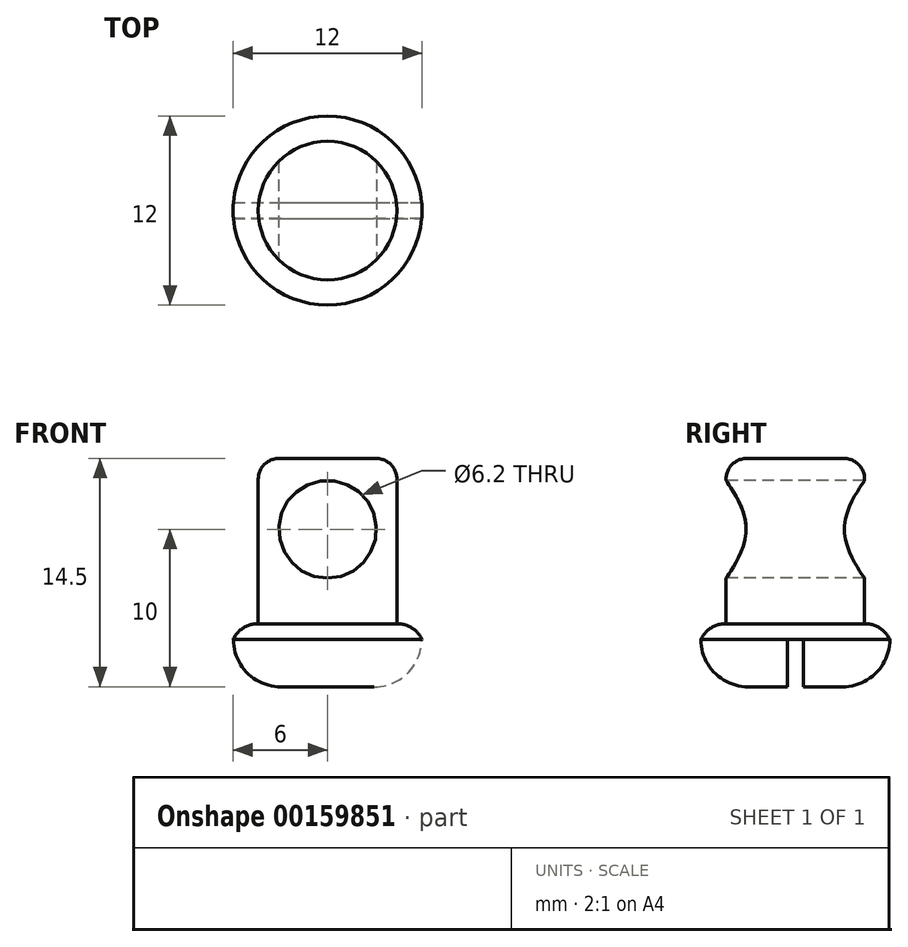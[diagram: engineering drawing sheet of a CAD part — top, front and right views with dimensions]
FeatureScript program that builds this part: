
annotation { "Feature Type Name" : "Feature", "Feature Type Description" : "" }
export const myFeature = defineFeature(function(context is Context, id is Id, definition is map)
    precondition{}
    {
        {
            var Q0;
            Q0=qCreatedBy(makeId("Top.planeOp"),FACE);
            var sketch = newSketch(context, id + "F0", { "sketchPlane" : qUnion([Q0])});
            skCircle(sketch, "E0", {"center": v(0, 0) * mm, "radius": 4.4 * mm});
            skCircle(sketch, "E1", {"center": v(0, 0) * mm, "radius": 6 * mm});
            skLineSegment(sketch, "E2", {"start": v(-5.98, 0.5) * mm, "end": v(5.98, 0.5) * mm});
            skLineSegment(sketch, "E3.MirrorCS", {"start": v(-5.98, -0.5) * mm, "end": v(5.98, -0.5) * mm});
            skSolve(sketch);
        }
        {
            var Q0;
            {var subQ0=sQuery(id+"F0.wireOp",EDGE,"E2");var subQ1=sQuery(id+"F0.wireOp",EDGE,"E0");var subQ2=makeQuery(id+"F0.imprint","INTERSECT",VERTEX,{"disambiguationData":[OD(0.0)],"derivedFrom":[subQ1,subQ0]});Q0=makeQuery(id+"F0.imprint","IMPRINT",FACE,{"disambiguationData":[TD([[makeQuery(id+"F0.imprint","IMPRINT",EDGE,{"disambiguationData":[TD([[subQ2,-1.0]])],"derivedFrom":subQ1}),1.0]])]});}
            var Q1;
            {var subQ0=sQuery(id+"F0.wireOp",EDGE,"E2");var subQ1=sQuery(id+"F0.wireOp",EDGE,"E0");var subQ2=makeQuery(id+"F0.imprint","INTERSECT",VERTEX,{"disambiguationData":[OD(0.0)],"derivedFrom":[subQ1,subQ0]});Q1=makeQuery(id+"F0.imprint","IMPRINT",FACE,{"disambiguationData":[TD([[makeQuery(id+"F0.imprint","IMPRINT",EDGE,{"disambiguationData":[TD([[subQ2,1.0]])],"derivedFrom":subQ1}),1.0]])]});}
            var Q2;
            {var subQ0=sQuery(id+"F0.wireOp",EDGE,"E3.MirrorCS");var subQ1=sQuery(id+"F0.wireOp",EDGE,"E0");var subQ2=makeQuery(id+"F0.imprint","INTERSECT",VERTEX,{"disambiguationData":[OD(0.0)],"derivedFrom":[subQ1,subQ0]});Q2=makeQuery(id+"F0.imprint","IMPRINT",FACE,{"disambiguationData":[TD([[makeQuery(id+"F0.imprint","IMPRINT",EDGE,{"disambiguationData":[TD([[subQ2,-1.0]])],"derivedFrom":subQ1}),1.0]])]});}
            extrude(context, id + "F1", {"entities" : qUnion([Q0, Q1, Q2]), "depth" : 14.5 * mm});
        }
        {
            var Q0;
            {var subQ0=sQuery(id+"F0.wireOp",EDGE,"E2");var subQ1=sQuery(id+"F0.wireOp",EDGE,"E0");var subQ2=makeQuery(id+"F0.imprint","INTERSECT",VERTEX,{"disambiguationData":[OD(0.0)],"derivedFrom":[subQ1,subQ0]});Q0=makeQuery(id+"F0.imprint","IMPRINT",FACE,{"disambiguationData":[TD([[makeQuery(id+"F0.imprint","IMPRINT",EDGE,{"disambiguationData":[TD([[subQ2,-1.0]])],"derivedFrom":subQ1}),-1.0]])]});}
            var Q1;
            {var subQ0=sQuery(id+"F0.wireOp",EDGE,"E3.MirrorCS");var subQ1=sQuery(id+"F0.wireOp",EDGE,"E0");var subQ2=makeQuery(id+"F0.imprint","INTERSECT",VERTEX,{"disambiguationData":[OD(0.0)],"derivedFrom":[subQ1,subQ0]});Q1=makeQuery(id+"F0.imprint","IMPRINT",FACE,{"disambiguationData":[TD([[makeQuery(id+"F0.imprint","IMPRINT",EDGE,{"disambiguationData":[TD([[subQ2,-1.0]])],"derivedFrom":subQ1}),-1.0]])]});}
            var Q2;
            {var subQ0=sQuery(id+"F0.wireOp",EDGE,"E2");var subQ1=sQuery(id+"F0.wireOp",EDGE,"E0");var subQ2=makeQuery(id+"F0.imprint","INTERSECT",VERTEX,{"disambiguationData":[OD(1.0)],"derivedFrom":[subQ1,subQ0]});Q2=makeQuery(id+"F0.imprint","IMPRINT",FACE,{"disambiguationData":[TD([[makeQuery(id+"F0.imprint","IMPRINT",EDGE,{"disambiguationData":[TD([[subQ2,1.0]])],"derivedFrom":subQ1}),-1.0]])]});}
            var Q3;
            {var subQ0=sQuery(id+"F0.wireOp",EDGE,"E2");var subQ1=sQuery(id+"F0.wireOp",EDGE,"E0");var subQ2=makeQuery(id+"F0.imprint","INTERSECT",VERTEX,{"disambiguationData":[OD(0.0)],"derivedFrom":[subQ1,subQ0]});Q3=makeQuery(id+"F0.imprint","IMPRINT",FACE,{"disambiguationData":[TD([[makeQuery(id+"F0.imprint","IMPRINT",EDGE,{"disambiguationData":[TD([[subQ2,1.0]])],"derivedFrom":subQ1}),-1.0]])]});}
            extrude(context, id + "F2", {"entities" : qUnion([Q0, Q1, Q2, Q3]), "operationType" : NewBodyOperationType.ADD, "depth" : 4 * mm});
        }
        {
            var Q0;
            {var subQ0=sQuery(id+"F0.wireOp",EDGE,"E2");var subQ1=sQuery(id+"F0.wireOp",EDGE,"E0");var subQ2=makeQuery(id+"F0.imprint","INTERSECT",VERTEX,{"disambiguationData":[OD(0.0)],"derivedFrom":[subQ1,subQ0]});Q0=makeQuery(id+"F0.imprint","IMPRINT",FACE,{"disambiguationData":[TD([[makeQuery(id+"F0.imprint","IMPRINT",EDGE,{"disambiguationData":[TD([[subQ2,-1.0]])],"derivedFrom":subQ1}),-1.0]])]});}
            var Q1;
            {var subQ0=sQuery(id+"F0.wireOp",EDGE,"E2");var subQ1=sQuery(id+"F0.wireOp",EDGE,"E0");var subQ2=makeQuery(id+"F0.imprint","INTERSECT",VERTEX,{"disambiguationData":[OD(0.0)],"derivedFrom":[subQ1,subQ0]});Q1=makeQuery(id+"F0.imprint","IMPRINT",FACE,{"disambiguationData":[TD([[makeQuery(id+"F0.imprint","IMPRINT",EDGE,{"disambiguationData":[TD([[subQ2,-1.0]])],"derivedFrom":subQ1}),1.0]])]});}
            var Q2;
            {var subQ0=sQuery(id+"F0.wireOp",EDGE,"E2");var subQ1=sQuery(id+"F0.wireOp",EDGE,"E0");var subQ2=makeQuery(id+"F0.imprint","INTERSECT",VERTEX,{"disambiguationData":[OD(1.0)],"derivedFrom":[subQ1,subQ0]});Q2=makeQuery(id+"F0.imprint","IMPRINT",FACE,{"disambiguationData":[TD([[makeQuery(id+"F0.imprint","IMPRINT",EDGE,{"disambiguationData":[TD([[subQ2,1.0]])],"derivedFrom":subQ1}),-1.0]])]});}
            extrude(context, id + "F3", {"entities" : qUnion([Q0, Q1, Q2]), "operationType" : NewBodyOperationType.REMOVE, "depth" : 3 * mm});
        }
        {
            var Q0;
            Q0=qCreatedBy(makeId("Front.planeOp"),FACE);
            cPlane(context, id + "F4", {"entities" : qUnion([Q0]), "cplaneType" : CPlaneType.OFFSET, "offset" : 4.75 * mm, "width" : 150 * mm, "height" : 150 * mm});
        }
        {
            var Q0;
            Q0=qCreatedBy(id+"F4.planeOp",FACE);
            var sketch = newSketch(context, id + "F5", { "sketchPlane" : qUnion([Q0])});
            skLineSegment(sketch, "E4.0", {"start": v(-6, 4) * mm, "end": v(6, 4) * mm, "construction": true});
            skCircle(sketch, "E5", {"center": v(0, 10) * mm, "radius": 3.1 * mm});
            skSolve(sketch);
        }
        {
            var Q0;
            Q0=makeQuery(id+"F5.imprint","IMPRINT",FACE,{"disambiguationData":[TD([[makeQuery(id+"F5.imprint","IMPRINT",EDGE,{"derivedFrom":sQuery(id+"F5.wireOp",EDGE,"E5")}),1.0]])]});
            extrude(context, id + "F6", {"entities" : qUnion([Q0]), "operationType" : NewBodyOperationType.REMOVE, "endBound" : BoundingType.THROUGH_ALL, "oppositeDirection" : true, "depth" : 25 * mm});
        }
        {
            var Q0;
            {var subQ1=sQuery(id+"F0.wireOp",EDGE,"E1");Q0=makeQuery(id+"F3.boolean.opBoolean","SPLIT",EDGE,{"disambiguationData":[TD([makeQuery(id+"F3.opExtrude","SWEPT_FACE",FACE,{"disambiguationData":[OSD([sQuery(id+"F0.wireOp",EDGE,"E2")])]})])],"derivedFrom":makeQuery(id+"F2.opExtrude","CAP_EDGE",EDGE,{"disambiguationData":[OSD([subQ1])],"isStart":true})});}
            var Q1;
            {var subQ1=sQuery(id+"F0.wireOp",EDGE,"E1");Q1=makeQuery(id+"F3.boolean.opBoolean","SPLIT",EDGE,{"disambiguationData":[TD([makeQuery(id+"F3.opExtrude","SWEPT_FACE",FACE,{"disambiguationData":[OSD([sQuery(id+"F0.wireOp",EDGE,"E3.MirrorCS")])]})])],"derivedFrom":makeQuery(id+"F2.opExtrude","CAP_EDGE",EDGE,{"disambiguationData":[OSD([subQ1])],"isStart":true})});}
            fillet(context, id + "F7", {"entities" : qUnion([Q0, Q1]), "radius" : 3 * mm, "tangentPropagation" : true, "allowEdgeOverflow" : false});
        }
        {
            var Q0;
            Q0=makeQuery(id+"F2.opExtrude","CAP_EDGE",EDGE,{"disambiguationData":[OSD([sQuery(id+"F0.wireOp",EDGE,"E1")])],"isStart":false});
            fillet(context, id + "F8", {"entities" : qUnion([Q0]), "radius" : 1.7 * mm, "tangentPropagation" : true, "allowEdgeOverflow" : false});
        }
        {
            var Q0;
            Q0=makeQuery(id+"F1.opExtrude","CAP_EDGE",EDGE,{"disambiguationData":[OSD([sQuery(id+"F0.wireOp",EDGE,"E0")])],"isStart":false});
            fillet(context, id + "F9", {"entities" : qUnion([Q0]), "radius" : 1.3 * mm, "tangentPropagation" : true, "allowEdgeOverflow" : false});
        }
    });
